# Revit family: Ladder_Vertical_KattsafeUSA_Caged_ParapetPlatform
name_source: partatom
category: Specialty Equipment
units: mm (PartAtom-declared; Revit-internal decimal feet)

## family parameters
Always vertical = Yes
Classification Number = 23.17.23.15
Cut with Voids When Loaded = No
Enable Cutting in Views = No
Maintain Annotation Orientation = No
Part Type = Normal
Room Calculation Point = No
Round Connector Dimension = Use Diameter
Shared = No
Work Plane-Based = No

## types (1)
- RL42
    Assembly Code = E1090100
    Default Elevation = 0' - 0"
    Description = Our RL42 configuration includes a Parapet platform. At the top, you’ll find a round knee rail constructed with the same high-tensile aluminum and mounted with screws. The mesh-style platform deck has a ribbed finish for enhanced safety.
    ElementType = Ladder
    Export Type to IFC As = IfcBuildingElementProxy
    IfcExportAs = IfcBuildingElementProxy
    IfcExportType = USERDEFINED
    Manufacturer = Kattsafe®
    ManufacturerOverallWidth = 3' - 0 1/2"
    ManufacturerSpecCode = RL42
    ManufacturerURLProductSpecific = https://kattsafe.com
    Material = Aluminum_Kattsafe_Satin
    Model = RL42
    ModifiedIssue = 20250822 $
    Type Comments = Ladder - Caged - Parapet Platform
    Type IFC Predefined Type = USERDEFINED
    URL = https://kattsafe.com
    Uniclass2015Code = Pr_25_30_85_02
    Uniclass2015Title = Access ladders
    Uniclass2015Version = Products v1.35

## geometry (parser evidence)
native form markers: Sweep x20
no freeform markers — native parametric forms only
